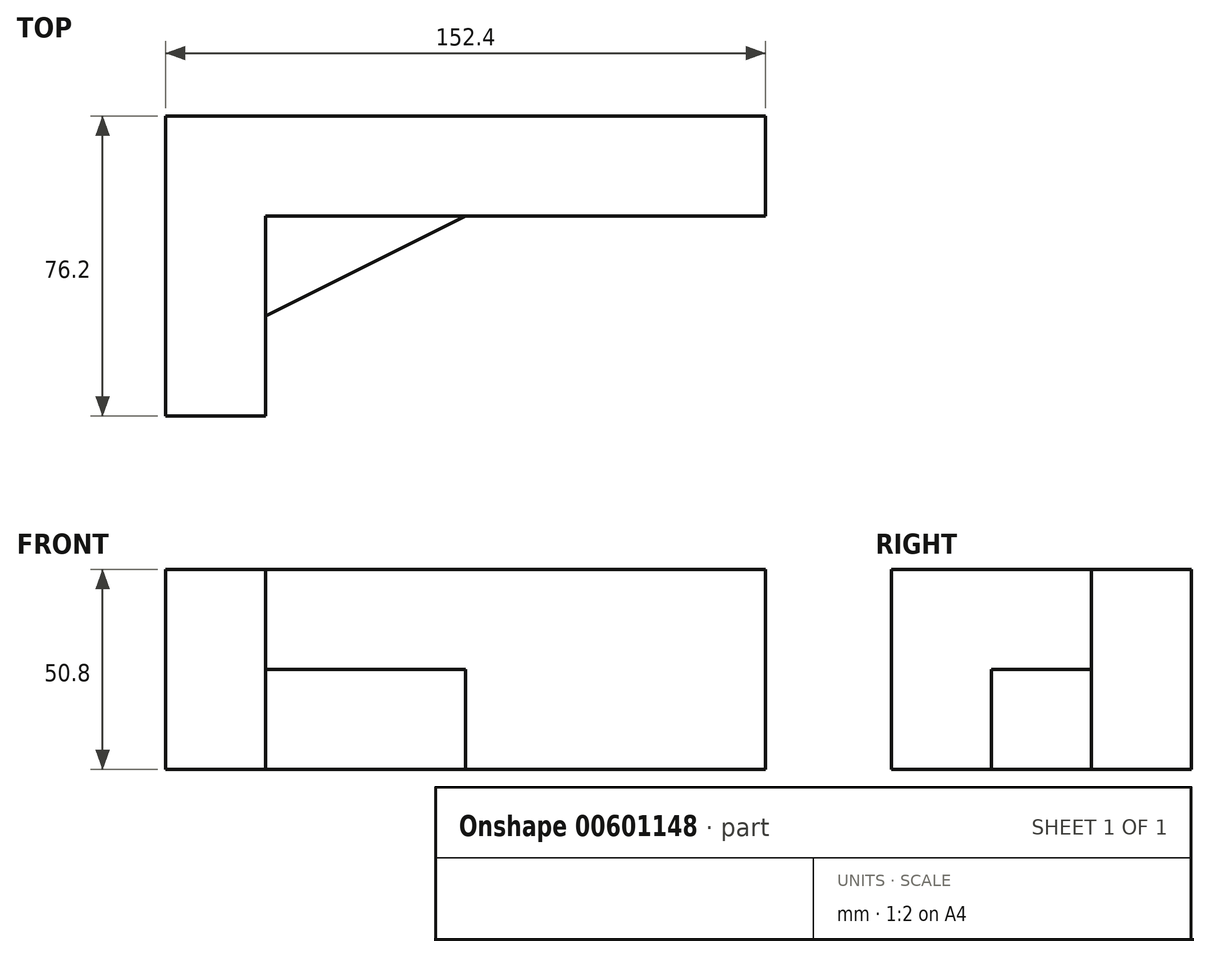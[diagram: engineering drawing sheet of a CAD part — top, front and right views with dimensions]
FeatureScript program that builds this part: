
annotation { "Feature Type Name" : "Feature", "Feature Type Description" : "" }
export const myFeature = defineFeature(function(context is Context, id is Id, definition is map)
    precondition{}
    {
        {
            var Q0;
            Q0=qCreatedBy(makeId("Top.planeOp"),FACE);
            var sketch = newSketch(context, id + "F0", { "sketchPlane" : qUnion([Q0])});
            skLineSegment(sketch, "E0", {"start": v(0, 0) * mm, "end": v(0, 76.2) * mm});
            skLineSegment(sketch, "E1", {"start": v(0, 76.2) * mm, "end": v(152.4, 76.2) * mm});
            skLineSegment(sketch, "E2", {"start": v(152.4, 76.2) * mm, "end": v(152.4, 50.8) * mm});
            skLineSegment(sketch, "E3", {"start": v(152.4, 50.8) * mm, "end": v(25.4, 50.8) * mm});
            skLineSegment(sketch, "E4", {"start": v(25.4, 50.8) * mm, "end": v(25.4, 0) * mm});
            skLineSegment(sketch, "E5", {"start": v(25.4, 0) * mm, "end": v(0, 0) * mm});
            skSolve(sketch);
        }
        {
            var Q0;
            Q0 = qSketchRegion(id + "F0", true);
            extrude(context, id + "F1", {"entities" : qUnion([Q0]), "depth" : 50.8 * mm, "offsetDistance" : 25.4 * mm});
        }
        {
            var Q0;
            Q0=makeQuery(id+"F1.opExtrude","CAP_FACE",FACE,{"disambiguationData":[OSD([sQuery(id+"F0.wireOp",EDGE,"E0"),sQuery(id+"F0.wireOp",EDGE,"E1"),sQuery(id+"F0.wireOp",EDGE,"E2"),sQuery(id+"F0.wireOp",EDGE,"E3"),sQuery(id+"F0.wireOp",EDGE,"E4"),sQuery(id+"F0.wireOp",EDGE,"E5")])],"isStart":true});
            var sketch = newSketch(context, id + "F2", { "sketchPlane" : qUnion([Q0])});
            skLineSegment(sketch, "E6", {"start": v(76.2, -50.8) * mm, "end": v(25.4, -25.4) * mm});
            skLineSegment(sketch, "E7", {"start": v(25.4, -25.4) * mm, "end": v(25.4, -50.8) * mm});
            skLineSegment(sketch, "E8", {"start": v(25.4, -50.8) * mm, "end": v(76.2, -50.8) * mm});
            skSolve(sketch);
        }
        {
            var Q0;
            Q0=makeQuery(id+"F2.imprint","IMPRINT",FACE,{"disambiguationData":[TD([[makeQuery(id+"F2.imprint","IMPRINT",EDGE,{"derivedFrom":sQuery(id+"F2.wireOp",EDGE,"E6")}),1.0]])]});
            extrude(context, id + "F3", {"entities" : qUnion([Q0]), "operationType" : NewBodyOperationType.ADD, "oppositeDirection" : true, "depth" : 25.4 * mm, "offsetDistance" : 25.4 * mm});
        }
    });
